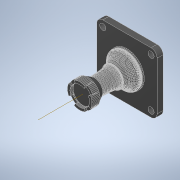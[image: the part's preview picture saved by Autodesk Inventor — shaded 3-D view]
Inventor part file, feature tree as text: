
AUTODESK INVENTOR PART (.ipt)
format: ipt  version: 2022 (Build 260153000, 153)  size: 6,067,712 bytes
history: native  units: mm
features: other x5, sketch x2, move_body x1, extrude x1, chamfer x1, revolve x1, projected_geometry x1
ambient origin geometry x8: Origin, YZ Plane, XZ Plane, XY Plane, X Axis, Y Axis, Z Axis, Center Point
bodies: Solid2 (feature_tree), Solid1 (feature_tree)
feature tree (12):
  other  "Queen Mold.ipt"
  other  "MeshFeature1"
  move_body  "Move Body1"
  extrude  "Extrusion1"  [1 undecoded]
  chamfer  "Chamfer1"  Distance=4.0mm
  revolve  "Revolution1"  Angle=45.0deg
  other  "Solid2::Queen Mold.ipt"
  other  "TaggingFeature1"
  other  "Work Axis1"
  sketch  "Sketch1"  dims[d0=10.0mm d1=-149.752mm d2=-92.942mm d3=-20.579778mm d4=4.0mm d5=0.0mm]
  projected_geometry  "Projected Loop1"
  sketch  "Sketch2"  dims[d6=1.0mm d7=2.0mm d8=45.0deg d9=45.0deg d10=90.0deg]
note: 1 required parameter value undecoded (feature->parameter linkage not recoverable at this tier; creation-order binding heuristic only, values carry confidence <= 0.55)
